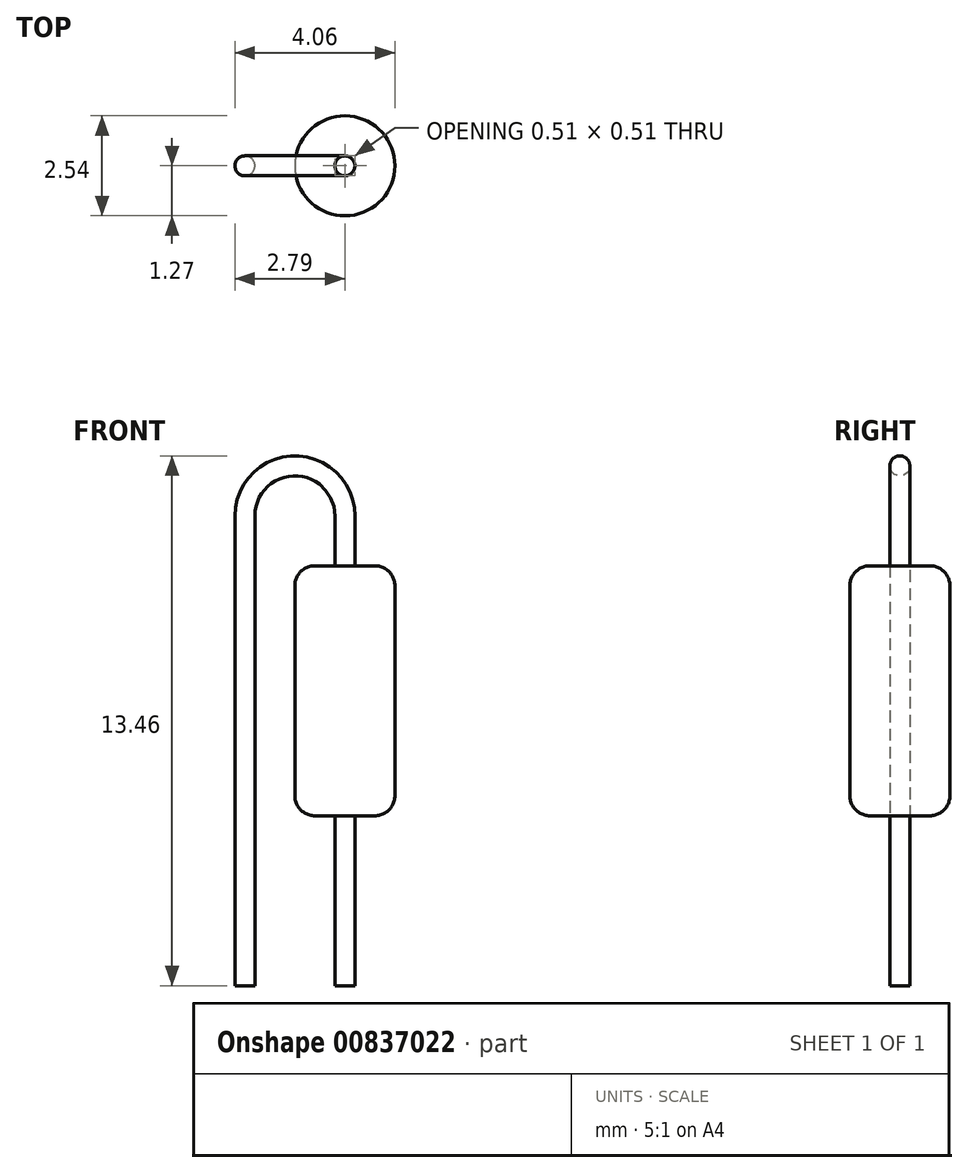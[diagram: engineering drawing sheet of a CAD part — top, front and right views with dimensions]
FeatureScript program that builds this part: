
annotation { "Feature Type Name" : "Feature", "Feature Type Description" : "" }
export const myFeature = defineFeature(function(context is Context, id is Id, definition is map)
    precondition{}
    {
        {
            var Q0;
            Q0=qCreatedBy(makeId("Front.planeOp"),FACE);
            var sketch = newSketch(context, id + "F0", { "sketchPlane" : qUnion([Q0])});
            skLineSegment(sketch, "E0.bottom", {"start": v(0, 0.5) * mm, "end": v(1.27, 0.5) * mm});
            skLineSegment(sketch, "E0.top", {"start": v(0, 6.86) * mm, "end": v(1.27, 6.86) * mm});
            skLineSegment(sketch, "E0.left", {"start": v(0, 0.5) * mm, "end": v(0, 6.86) * mm});
            skLineSegment(sketch, "E0.right", {"start": v(1.27, 0.5) * mm, "end": v(1.27, 6.86) * mm});
            skSolve(sketch);
        }
        {
            var Q0;
            Q0 = qSketchRegion(id + "F0", true);
            var Q1;
            Q1=sQuery(id+"F0.wireOp",EDGE,"E0.left");
            revolve(context, id + "F1", {"surfaceOperationType" : NewSurfaceOperationType.NEW, "entities" : qUnion([Q0]), "axis" : qUnion([Q1]), "revolveType" : RevolveType.FULL});
        }
        {
            var Q0;
            Q0=makeQuery(id+"F1.opRevolve","SWEPT_EDGE",EDGE,{"disambiguationData":[OSD([sQuery(id+"F0.wireOp",EDGE,"E0.top"),sQuery(id+"F0.wireOp",EDGE,"E0.right")])]});
            var Q1;
            Q1=makeQuery(id+"F1.opRevolve","SWEPT_EDGE",EDGE,{"disambiguationData":[OSD([sQuery(id+"F0.wireOp",EDGE,"E0.bottom"),sQuery(id+"F0.wireOp",EDGE,"E0.right")])]});
            fillet(context, id + "F2", {"entities" : qUnion([Q0, Q1]), "radius" : 0.5 * mm, "tangentPropagation" : true, "allowEdgeOverflow" : false});
        }
        {
            var Q0;
            Q0=qCreatedBy(makeId("Front.planeOp"),FACE);
            var sketch = newSketch(context, id + "F3", { "sketchPlane" : qUnion([Q0])});
            skLineSegment(sketch, "E1", {"start": v(0, -3.81) * mm, "end": v(0, 8.13) * mm});
            skLineSegment(sketch, "E2", {"start": v(-2.54, 8.13) * mm, "end": v(-2.54, -3.81) * mm});
            skLineSegment(sketch, "E3", {"start": v(-2.54, -3.81) * mm, "end": v(0, -3.81) * mm, "construction": true});
            skArc(sketch, "E4", {"start": v(0, 8.13) * mm, "mid": v(-1.27, 9.4) * mm, "end": v(-2.54, 8.13) * mm});
            skSolve(sketch);
        }
        {
            var Q0;
            Q0=qCreatedBy(makeId("Top.planeOp"),FACE);
            cPlane(context, id + "F4", {"entities" : qUnion([Q0]), "cplaneType" : CPlaneType.OFFSET, "offset" : 3.8 * mm, "oppositeDirection" : true, "width" : 152.4 * mm, "height" : 152.4 * mm});
        }
        {
            var Q0;
            Q0=qCreatedBy(id+"F4.planeOp",FACE);
            var sketch = newSketch(context, id + "F5", { "sketchPlane" : qUnion([Q0])});
            skCircle(sketch, "E5", {"center": v(0, 0) * mm, "radius": 0.25 * mm});
            skSolve(sketch);
        }
        {
            var Q0;
            Q0 = qSketchRegion(id + "F5", true);
            var Q1;
            Q1 = qConstructionFilter(qBodyType(qCreatedBy(id + "F3" ,EDGE), BodyType.WIRE), ConstructionObject.NO);
            sweep(context, id + "F6", {"operationType" : NewBodyOperationType.ADD, "profiles" : qUnion([Q0]), "path" : qUnion([Q1])});
        }
    });
